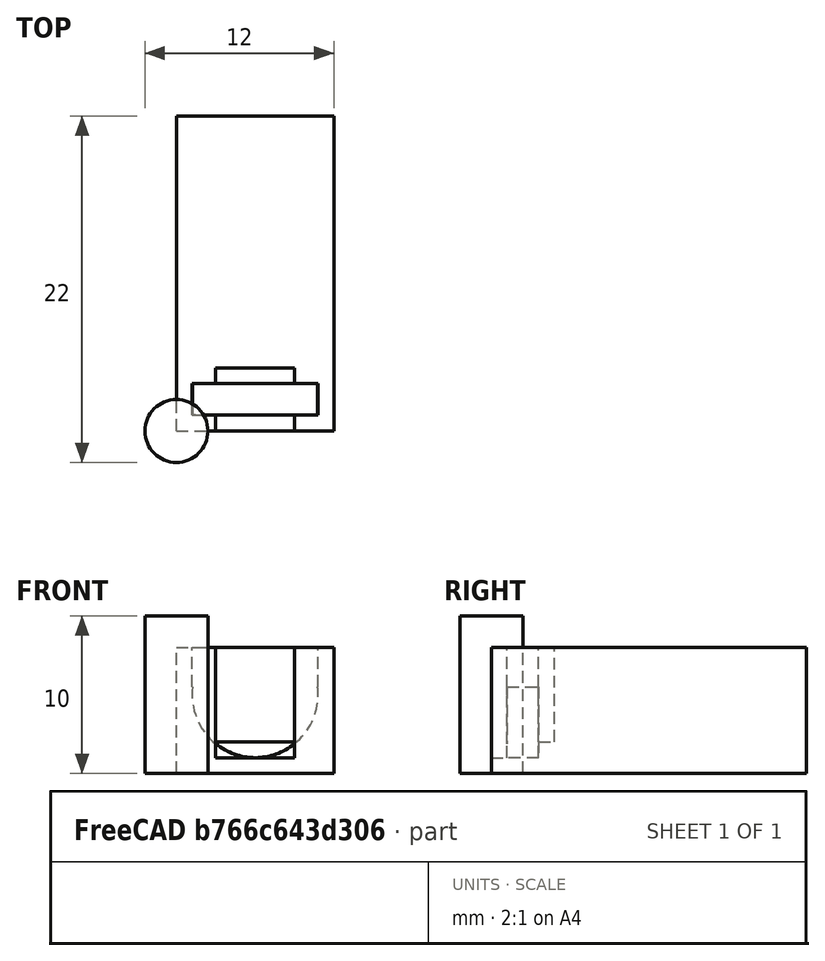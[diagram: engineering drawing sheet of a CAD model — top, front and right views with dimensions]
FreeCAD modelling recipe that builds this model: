
FCSTD DOCUMENT  (FreeCAD 0.16R4924 (Git))
Label: pin_v2
License: All rights reserved
LicenseURL: http://en.wikipedia.org/wiki/All_rights_reserved
objects: Part::Box×4, Part::Cut×4, Part::Cylinder×2, App::MeasureDistance×2
note: 10 computed .brp shape members not serialized (recipe doc carries the construction recipe); baked Part::Feature solids carry a one-line shape summary decoded from their .brp

FEATURE [Part::Box] Box  label="pin"
  Height = 8
  Length = 10
  Width = 20
FEATURE [Part::Cylinder] Cylinder  label="solenoid_head_slot"
  Angle = 360
  Height = 2
  Placement = pos=(5,3,5) rot=(1,0,0;1.5708rad)
  Radius = 4
FEATURE [Part::Cut] Cut
  Base = -> Box
  Tool = -> Cylinder
FEATURE [Part::Box] Box001  label="end_opening"
  Height = 7
  Length = 5
  Placement = pos=(2.5,0,1) rot=(0,0,1;0rad)
  Width = 1
FEATURE [Part::Cut] Cut001
  Base = -> Cut
  Tool = -> Box001
FEATURE [Part::Box] Box002  label="interior_opening"
  Height = 6
  Length = 5
  Placement = pos=(2.5,3,2) rot=(0,0,1;0rad)
  Width = 1
FEATURE [Part::Cut] Cut002
  Base = -> Cut001
  Tool = -> Box002
FEATURE [Part::Box] Box003  label="cylinder_edge_refinement"
  Height = 2.5
  Length = 8
  Placement = pos=(1,1,5.5) rot=(0,0,1;0rad)
  Width = 2
FEATURE [Part::Cut] Cut003
  Base = -> Cut002
  Tool = -> Box003
FEATURE [App::MeasureDistance] Distance  label="Distance: 9.935"
  Distance = 9.93546
  P1 = (0,4.11934,8)
  P2 = (9.93226,4.37128,8)
FEATURE [App::MeasureDistance] Distance001  label="Distance: 19.946"
  Distance = 19.9461
  P1 = (10,0.0544001,8)
  P2 = (10,20,7.85638)
FEATURE [Part::Cylinder] Cylinder001  label="rounded_top"
  Angle = 360
  Height = 10
  Radius = 2
